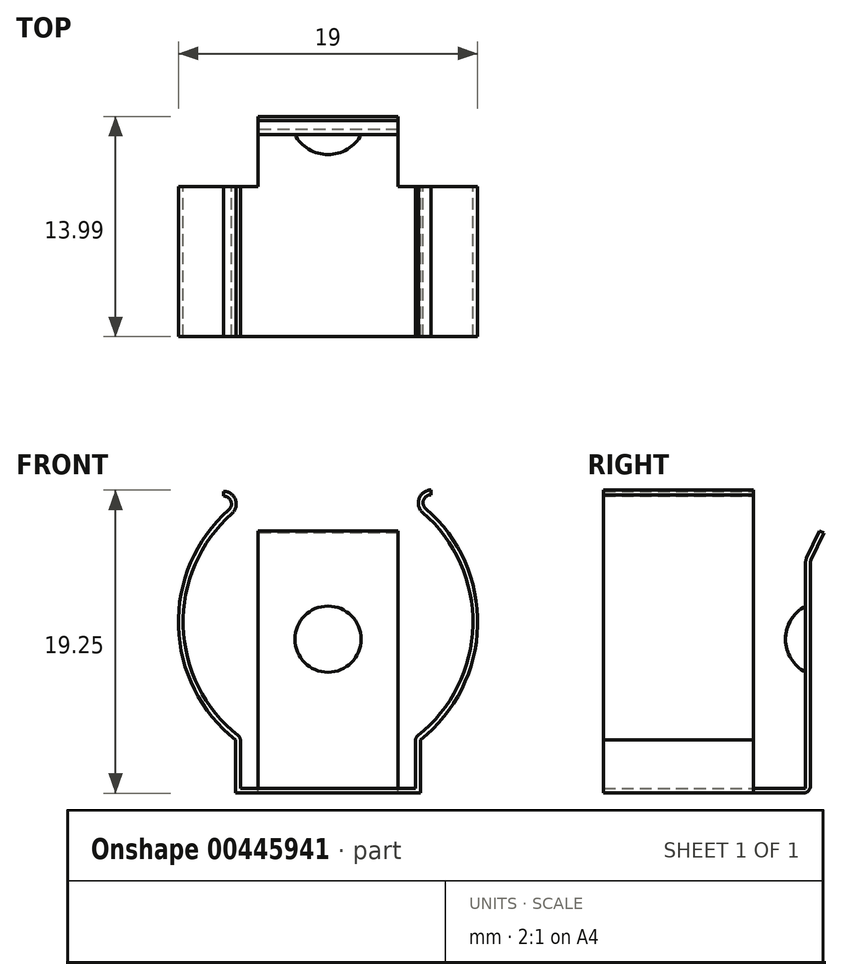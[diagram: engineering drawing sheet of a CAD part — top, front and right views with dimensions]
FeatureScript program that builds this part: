
annotation { "Feature Type Name" : "Feature", "Feature Type Description" : "" }
export const myFeature = defineFeature(function(context is Context, id is Id, definition is map)
    precondition{}
    {
        {
            var Q0;
            Q0=qCreatedBy(makeId("Front.planeOp"),FACE);
            var sketch = newSketch(context, id + "F0", { "sketchPlane" : qUnion([Q0])});
            skArc(sketch, "E0", {"start": v(-6.1, 6.89) * mm, "mid": v(-9.2, -0.26) * mm, "end": v(-5.7, -7.22) * mm});
            skArc(sketch, "E1", {"start": v(-6.1, 6.89) * mm, "mid": v(-5.88, 7.78) * mm, "end": v(-6.64, 8.3) * mm});
            skArc(sketch, "E2", {"start": v(6.55, 8.38) * mm, "mid": v(5.79, 7.86) * mm, "end": v(6.02, 6.96) * mm});
            skPoint(sketch, "E3.endSnap0", {"position": v(0, -10.56) * mm});
            skLineSegment(sketch, "E4", {"start": v(-5.56, -9.92) * mm, "end": v(-5.56, -10.56) * mm});
            skLineSegment(sketch, "E5", {"start": v(-5.56, -10.56) * mm, "end": v(5.56, -10.56) * mm});
            skLineSegment(sketch, "E6", {"start": v(5.56, -10.56) * mm, "end": v(5.56, -10.56) * mm});
            skLineSegment(sketch, "E7", {"start": v(5.56, -10.56) * mm, "end": v(5.56, -7.51) * mm});
            skLineSegment(sketch, "E8", {"start": v(-5.56, -9.92) * mm, "end": v(-5.56, -7.51) * mm});
            skArc(sketch, "E9", {"start": v(5.7, -7.22) * mm, "mid": v(5.6, -7.35) * mm, "end": v(5.56, -7.51) * mm});
            skArc(sketch, "E10", {"start": v(-5.56, -7.51) * mm, "mid": v(-5.6, -7.35) * mm, "end": v(-5.7, -7.22) * mm});
            skArc(sketch, "E11.trimOffspring", {"start": v(5.7, -7.22) * mm, "mid": v(9.2, -0.2) * mm, "end": v(6.02, 6.96) * mm});
            skArc(sketch, "E12.0", {"start": v(-6.3, 7.11) * mm, "mid": v(-6.17, 7.67) * mm, "end": v(-6.64, 8) * mm});
            skArc(sketch, "E12.1", {"start": v(-6.3, 7.11) * mm, "mid": v(-9.5, -0.28) * mm, "end": v(-5.87, -7.48) * mm});
            skLineSegment(sketch, "E12.2", {"start": v(-5.87, -9.92) * mm, "end": v(-5.87, -7.48) * mm});
            skLineSegment(sketch, "E12.3", {"start": v(-5.87, -9.92) * mm, "end": v(-5.87, -10.87) * mm});
            skArc(sketch, "E12.4", {"start": v(6.55, 8.08) * mm, "mid": v(6.07, 7.75) * mm, "end": v(6.22, 7.2) * mm});
            skArc(sketch, "E12.5", {"start": v(5.87, -7.48) * mm, "mid": v(9.5, -0.23) * mm, "end": v(6.22, 7.2) * mm});
            skLineSegment(sketch, "E12.6", {"start": v(5.87, -10.87) * mm, "end": v(5.87, -7.48) * mm});
            skLineSegment(sketch, "E12.7", {"start": v(-5.87, -10.87) * mm, "end": v(5.87, -10.87) * mm});
            skLineSegment(sketch, "E13", {"start": v(-6.64, 8.3) * mm, "end": v(-6.64, 8) * mm});
            skLineSegment(sketch, "E14", {"start": v(6.55, 8.38) * mm, "end": v(6.55, 8.08) * mm});
            skSolve(sketch);
        }
        {
            var Q0;
            Q0 = qSketchRegion(id + "F0", true);
            extrude(context, id + "F1", {"entities" : qUnion([Q0]), "depth" : 9.52 * mm});
        }
        {
            var Q0;
            Q0=qCreatedBy(makeId("Right.planeOp"),FACE);
            var sketch = newSketch(context, id + "F2", { "sketchPlane" : qUnion([Q0])});
            skLineSegment(sketch, "E15", {"start": v(0, -10.87) * mm, "end": v(3.16, -10.87) * mm});
            skArc(sketch, "E16", {"start": v(3.16, -10.87) * mm, "mid": v(3.48, -10.74) * mm, "end": v(3.6, -10.42) * mm});
            skLineSegment(sketch, "E17", {"start": v(3.6, -10.42) * mm, "end": v(3.6, 3.75) * mm});
            skArc(sketch, "E18", {"start": v(3.65, 3.94) * mm, "mid": v(3.62, 3.84) * mm, "end": v(3.6, 3.75) * mm});
            skLineSegment(sketch, "E19", {"start": v(3.65, 3.94) * mm, "end": v(4.46, 5.67) * mm});
            skCircle(sketch, "E20", {"center": v(4.4, -1.09) * mm, "radius": 2.37 * mm, "construction": true});
            skLineSegment(sketch, "E21.0", {"start": v(3.37, 4.07) * mm, "end": v(4.18, 5.8) * mm});
            skArc(sketch, "E21.1", {"start": v(3.37, 4.07) * mm, "mid": v(3.32, 3.91) * mm, "end": v(3.3, 3.75) * mm});
            skLineSegment(sketch, "E21.2", {"start": v(3.3, -10.56) * mm, "end": v(3.3, 3.75) * mm});
            skLineSegment(sketch, "E21.3", {"start": v(0, -10.56) * mm, "end": v(3.3, -10.56) * mm});
            skLineSegment(sketch, "E22", {"start": v(4.46, 5.67) * mm, "end": v(4.18, 5.8) * mm});
            skLineSegment(sketch, "E23", {"start": v(0, -10.87) * mm, "end": v(0, -10.56) * mm});
            skSolve(sketch);
        }
        {
            var Q0;
            Q0 = qSketchRegion(id + "F2", true);
            extrude(context, id + "F3", {"entities" : qUnion([Q0]), "operationType" : NewBodyOperationType.ADD, "endBound" : BoundingType.SYMMETRIC, "depth" : 8.9 * mm});
        }
        {
            var Q0;
            Q0=qCreatedBy(makeId("Right.planeOp"),FACE);
            var sketch = newSketch(context, id + "F4", { "sketchPlane" : qUnion([Q0])});
            skArc(sketch, "E24", {"start": v(2.03, -1.09) * mm, "mid": v(2.37, -2.32) * mm, "end": v(3.3, -3.2) * mm});
            skLineSegment(sketch, "E25", {"start": v(3.3, -1.09) * mm, "end": v(3.3, -3.2) * mm});
            skLineSegment(sketch, "E26", {"start": v(3.3, -1.09) * mm, "end": v(2.03, -1.09) * mm});
            skPoint(sketch, "E27.orphan", {"position": v(3.3, 1.01) * mm});
            skSolve(sketch);
        }
        {
            var Q0;
            Q0=makeQuery(id+"F4.imprint","IMPRINT",FACE,{"disambiguationData":[TD([[makeQuery(id+"F4.imprint","IMPRINT",EDGE,{"derivedFrom":sQuery(id+"F4.wireOp",EDGE,"E24")}),1.0]])]});
            var Q1;
            Q1=sQuery(id+"F4.wireOp",EDGE,"E26");
            revolve(context, id + "F5", {"operationType" : NewBodyOperationType.ADD, "entities" : qUnion([Q0]), "axis" : qUnion([Q1]), "revolveType" : RevolveType.FULL});
        }
    });
